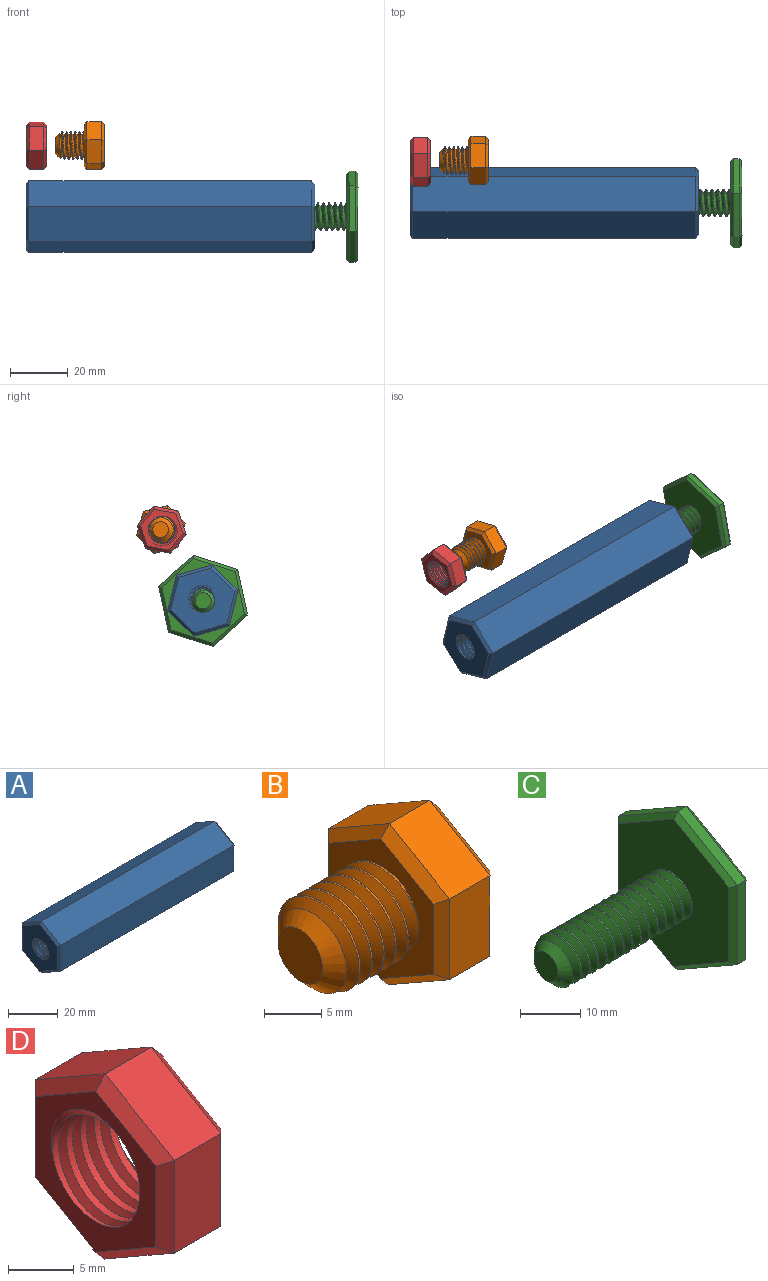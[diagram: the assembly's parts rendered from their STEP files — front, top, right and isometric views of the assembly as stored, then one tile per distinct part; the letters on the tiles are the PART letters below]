
ASSEMBLY  parts=4 mates=2
PART A: 23 faces, bbox 102.3x22.6x26 mm
  f0: cylinder r=4.12mm len=100mm, axis (1,0,0), area 1511.6mm2, adj f7,f8,f21,f22
  f1: plane 98x10.98mm, normal (0,-0.5,0.86), area 1244.8mm2, adj f2,f6,f14,f18
  f2: plane 98x12.7mm, normal (0,-1,0), area 1244.8mm2, adj f1,f3,f12,f16
  f3: plane 98x11.02mm, normal (0,-0.5,-0.87), area 1244.8mm2, adj f2,f4,f10,f15
  f4: plane 98x10.98mm, normal (0,0.5,-0.86), area 1244.8mm2, adj f3,f5,f9,f17
  f5: plane 98x12.7mm, normal (0,1,0), area 1244.8mm2, adj f4,f6,f11,f19
  f6: plane 98x11.02mm, normal (0,0.5,0.87), area 1244.8mm2, adj f1,f5,f13,f20
  f7: plane 23.7x20.63mm, normal (-1,0,0), area 282.8mm2, adj f0,f9,f10,f11,f12,f13,f14,f21
  f8: plane 23.7x20.63mm, normal (1,0,0), area 282.8mm2, adj f0,f15,f16,f17,f18,f19,f20,f21
  f9: plane 10.99x6.96mm, normal (-0.71,0.36,-0.61), area 17.1mm2, adj f4,f7,f10,f11
  f10: plane 11.02x6.9mm, normal (-0.71,-0.35,-0.61), area 17.1mm2, adj f3,f7,f9,f12
  f11: plane 12.7x1.03mm, normal (-0.71,0.71,0), area 17.1mm2, adj f5,f7,f9,f13
  f12: plane 12.7x1.03mm, normal (-0.71,-0.71,0), area 17.1mm2, adj f2,f7,f10,f14
  f13: plane 11.02x6.9mm, normal (-0.71,0.35,0.61), area 17.1mm2, adj f6,f7,f11,f14
  f14: plane 10.99x6.96mm, normal (-0.71,-0.36,0.61), area 17.1mm2, adj f1,f7,f12,f13
  f15: plane 11.02x6.9mm, normal (0.71,-0.35,-0.61), area 17.1mm2, adj f3,f8,f16,f17
  f16: plane 12.7x1.03mm, normal (0.71,-0.71,0), area 17.1mm2, adj f2,f8,f15,f18
  f17: plane 10.99x6.96mm, normal (0.71,0.36,-0.61), area 17.1mm2, adj f4,f8,f15,f19
  f18: plane 10.99x6.96mm, normal (0.71,-0.36,0.61), area 17.1mm2, adj f1,f8,f16,f20
  f19: plane 12.7x1.03mm, normal (0.71,0.71,0), area 17.1mm2, adj f5,f8,f17,f20
  f20: plane 11.02x6.9mm, normal (0.71,0.35,0.61), area 17.1mm2, adj f6,f8,f18,f19
  f21: bspline ~101.65x12.11mm, area 1923mm2, adj f0,f7,f8,f22
  f22: bspline ~101.32x12.11mm, area 1923.1mm2, adj f0,f7,f8,f21
PART B: 25 faces, bbox 17.8x15.9x18.1 mm
  f0: cylinder r=4.75mm len=9.5mm, axis (1,0,0), area 28.1mm2, adj f1,f2,f4,f12
  f1: bspline ~10.97x9.91mm, area 196.7mm2, adj f0,f2,f4,f12
  f2: bspline ~10.97x10.66mm, area 196.6mm2, adj f0,f1,f4,f12
  f3: plane 5.5x5.5mm, normal (-1,0,0), area 23.8mm2, adj f4
  f4: cone r=4.75mm half-angle=45deg, axis (1,0,0), area 47.4mm2, adj f0,f1,f2,f3
  f5: plane 7.48x5mm, normal (0,-0.5,0.86), area 43.3mm2, adj f6,f10,f18,f22
  f6: plane 8.66x5mm, normal (0,-1,0), area 43.3mm2, adj f5,f7,f16,f20
  f7: plane 7.52x5mm, normal (0,-0.5,-0.87), area 43.3mm2, adj f6,f8,f14,f19
  f8: plane 7.48x5mm, normal (0,0.5,-0.86), area 43.3mm2, adj f7,f9,f13,f21
  f9: plane 8.66x5mm, normal (0,1,0), area 43.3mm2, adj f8,f10,f15,f23
  f10: plane 7.52x5mm, normal (0,0.5,0.87), area 43.3mm2, adj f5,f9,f17,f24
  f11: plane 15.01x13.03mm, normal (1,0,0), area 146.4mm2, adj f13,f14,f15,f16,f17,f18
  f12: plane 15.83x13.85mm, normal (-1,0,0), area 89.2mm2, adj f0,f1,f2,f19,f20,f21,f22,f23
  f13: plane 7.49x4.93mm, normal (0.71,0.36,-0.61), area 11.4mm2, adj f8,f11,f14,f15
  f14: plane 7.52x4.88mm, normal (0.71,-0.35,-0.61), area 11.4mm2, adj f7,f11,f13,f16
  f15: plane 8.66x1.03mm, normal (0.71,0.71,0), area 11.4mm2, adj f9,f11,f13,f17
  f16: plane 8.66x1.03mm, normal (0.71,-0.71,0), area 11.4mm2, adj f6,f11,f14,f18
  f17: plane 7.52x4.88mm, normal (0.71,0.35,0.61), area 11.4mm2, adj f10,f11,f15,f18
  f18: plane 7.49x4.93mm, normal (0.71,-0.36,0.61), area 11.4mm2, adj f5,f11,f16,f17
  f19: plane 7.52x4.88mm, normal (-0.71,-0.35,-0.61), area 11.4mm2, adj f7,f12,f20,f21
  f20: plane 8.66x1.03mm, normal (-0.71,-0.71,0), area 11.4mm2, adj f6,f12,f19,f22
  f21: plane 7.49x4.93mm, normal (-0.71,0.36,-0.61), area 11.4mm2, adj f8,f12,f19,f23
  f22: plane 7.49x4.93mm, normal (-0.71,-0.36,0.61), area 11.4mm2, adj f5,f12,f20,f24
  f23: plane 8.66x1.03mm, normal (-0.71,0.71,0), area 11.4mm2, adj f9,f12,f21,f24
  f24: plane 7.52x4.88mm, normal (-0.71,0.35,0.61), area 11.4mm2, adj f10,f12,f22,f23
PART C: 26 faces, bbox 35.6x29.1x33.4 mm
  f0: cylinder r=4.8mm len=28mm, axis (1,0,0), area 23.2mm2, adj f1,f2,f4,f5,f13
  f1: bspline ~30.88x11.09mm, area 638.9mm2, adj f0,f2,f4,f5,f13
  f2: bspline ~31.54x11.09mm, area 636.6mm2, adj f0,f1,f4,f13
  f3: plane 5.6x5.6mm, normal (-1,0,0), area 24.6mm2, adj f4
  f4: cone r=4.8mm half-angle=45deg, axis (1,0,0), area 41.8mm2, adj f0,f1,f2,f3,f5
  f5: cone r=4.8mm half-angle=45deg, axis (1,0,0), area 0.4mm2, adj f0,f1,f4
  f6: plane 13.98x8.12mm, normal (0,-0.5,0.86), area 32.3mm2, adj f7,f11,f19,f23
  f7: plane 16.17x2mm, normal (0,-1,0), area 32.3mm2, adj f6,f8,f17,f21
  f8: plane 14.02x8.05mm, normal (0,-0.5,-0.87), area 32.3mm2, adj f7,f9,f15,f20
  f9: plane 13.98x8.12mm, normal (0,0.5,-0.86), area 32.3mm2, adj f8,f10,f14,f22
  f10: plane 16.17x2mm, normal (0,1,0), area 32.3mm2, adj f9,f11,f16,f24
  f11: plane 14.02x8.05mm, normal (0,0.5,0.87), area 32.3mm2, adj f6,f10,f18,f25
  f12: plane 30.02x26.04mm, normal (1,0,0), area 585.4mm2, adj f14,f15,f16,f17,f18,f19
  f13: plane 31.1x27.12mm, normal (-1,0,0), area 531mm2, adj f0,f1,f2,f20,f21,f22,f23,f24
  f14: plane 13.98x8.69mm, normal (0.71,0.36,-0.61), area 22mm2, adj f9,f12,f15,f16
  f15: plane 14.02x8.63mm, normal (0.71,-0.35,-0.61), area 22mm2, adj f8,f12,f14,f17
  f16: plane 16.17x1.04mm, normal (0.71,0.71,0), area 22mm2, adj f10,f12,f14,f18
  f17: plane 16.17x1.04mm, normal (0.71,-0.71,0), area 22mm2, adj f7,f12,f15,f19
  f18: plane 14.02x8.63mm, normal (0.71,0.35,0.61), area 22mm2, adj f11,f12,f16,f19
  f19: plane 13.98x8.69mm, normal (0.71,-0.36,0.61), area 22mm2, adj f6,f12,f17,f18
  f20: plane 14.02x8.63mm, normal (-0.71,-0.35,-0.61), area 22mm2, adj f8,f13,f21,f22
  f21: plane 16.17x1.04mm, normal (-0.71,-0.71,0), area 22mm2, adj f7,f13,f20,f23
  f22: plane 13.98x8.69mm, normal (-0.71,0.36,-0.61), area 22mm2, adj f9,f13,f20,f24
  f23: plane 13.98x8.69mm, normal (-0.71,-0.36,0.61), area 22mm2, adj f6,f13,f21,f25
  f24: plane 16.17x1.04mm, normal (-0.71,0.71,0), area 22mm2, adj f10,f13,f22,f25
  f25: plane 14.02x8.63mm, normal (-0.71,0.35,0.61), area 22mm2, adj f11,f13,f23,f24
PART D: 23 faces, bbox 9.1x15.4x17.7 mm
  f0: plane 7.49x5mm, normal (0,-0.5,0.86), area 43.3mm2, adj f1,f5,f13,f17
  f1: plane 8.66x5mm, normal (0,-1,0), area 43.3mm2, adj f0,f2,f11,f15
  f2: plane 7.51x5mm, normal (0,-0.5,-0.87), area 43.3mm2, adj f1,f3,f9,f14
  f3: plane 7.49x5mm, normal (0,0.5,-0.86), area 43.3mm2, adj f2,f4,f8,f16
  f4: plane 8.66x5mm, normal (0,1,0), area 43.3mm2, adj f3,f5,f10,f18
  f5: plane 7.51x5mm, normal (0,0.5,0.87), area 43.3mm2, adj f0,f4,f12,f19
  f6: plane 15.37x13.38mm, normal (-1,0,0), area 71.4mm2, adj f8,f9,f10,f11,f12,f13,f20,f21
  f7: plane 15.37x13.38mm, normal (1,0,0), area 71.4mm2, adj f14,f15,f16,f17,f18,f19,f20,f21
  f8: plane 7.49x4.93mm, normal (-0.71,0.36,-0.61), area 11.4mm2, adj f3,f6,f9,f10
  f9: plane 7.51x4.89mm, normal (-0.71,-0.35,-0.61), area 11.4mm2, adj f2,f6,f8,f11
  f10: plane 8.66x1.02mm, normal (-0.71,0.71,0), area 11.4mm2, adj f4,f6,f8,f12
  f11: plane 8.66x1.02mm, normal (-0.71,-0.71,0), area 11.4mm2, adj f1,f6,f9,f13
  f12: plane 7.51x4.89mm, normal (-0.71,0.35,0.61), area 11.4mm2, adj f5,f6,f10,f13
  f13: plane 7.49x4.93mm, normal (-0.71,-0.36,0.61), area 11.4mm2, adj f0,f6,f11,f12
  f14: plane 7.51x4.89mm, normal (0.71,-0.35,-0.61), area 11.4mm2, adj f2,f7,f15,f16
  f15: plane 8.66x1.02mm, normal (0.71,-0.71,0), area 11.4mm2, adj f1,f7,f14,f17
  f16: plane 7.49x4.93mm, normal (0.71,0.36,-0.61), area 11.4mm2, adj f3,f7,f14,f18
  f17: plane 7.49x4.93mm, normal (0.71,-0.36,0.61), area 11.4mm2, adj f0,f7,f15,f19
  f18: plane 8.66x1.02mm, normal (0.71,0.71,0), area 11.4mm2, adj f4,f7,f16,f19
  f19: plane 7.51x4.89mm, normal (0.71,0.35,0.61), area 11.4mm2, adj f5,f7,f17,f18
  f20: cylinder r=4.66mm len=9.32mm, axis (1,0,0), area 85.4mm2, adj f6,f7,f21,f22
  f21: bspline ~12.5x10.82mm, area 128.4mm2, adj f6,f7,f20,f22
  f22: bspline ~12.5x10.82mm, area 128.5mm2, adj f6,f7,f20,f21
PLACE A rot(axis=(0,0.6,-0.8),180deg) t=(-55.27,-6.86,23.48)mm fixed
PLACE B rot(axis=(-1,0,0),43.8deg) t=(-31.66,7.73,48.08)mm
PLACE C rot(axis=(1,0,0),167.5deg) t=(57.73,-6.94,23.4)mm
PLACE D rot(axis=(1,0,0),100.2deg) t=(-48.16,7.38,48.02)mm fixed
MATE cylindrical C.f0 <-> A.f7  axis (-1,0,0) through (25.73,-6.94,23.4)mm
MATE cylindrical B.f0 <-> D.f6  axis (-1,0,0) through (-45.16,7.73,48.08)mm
